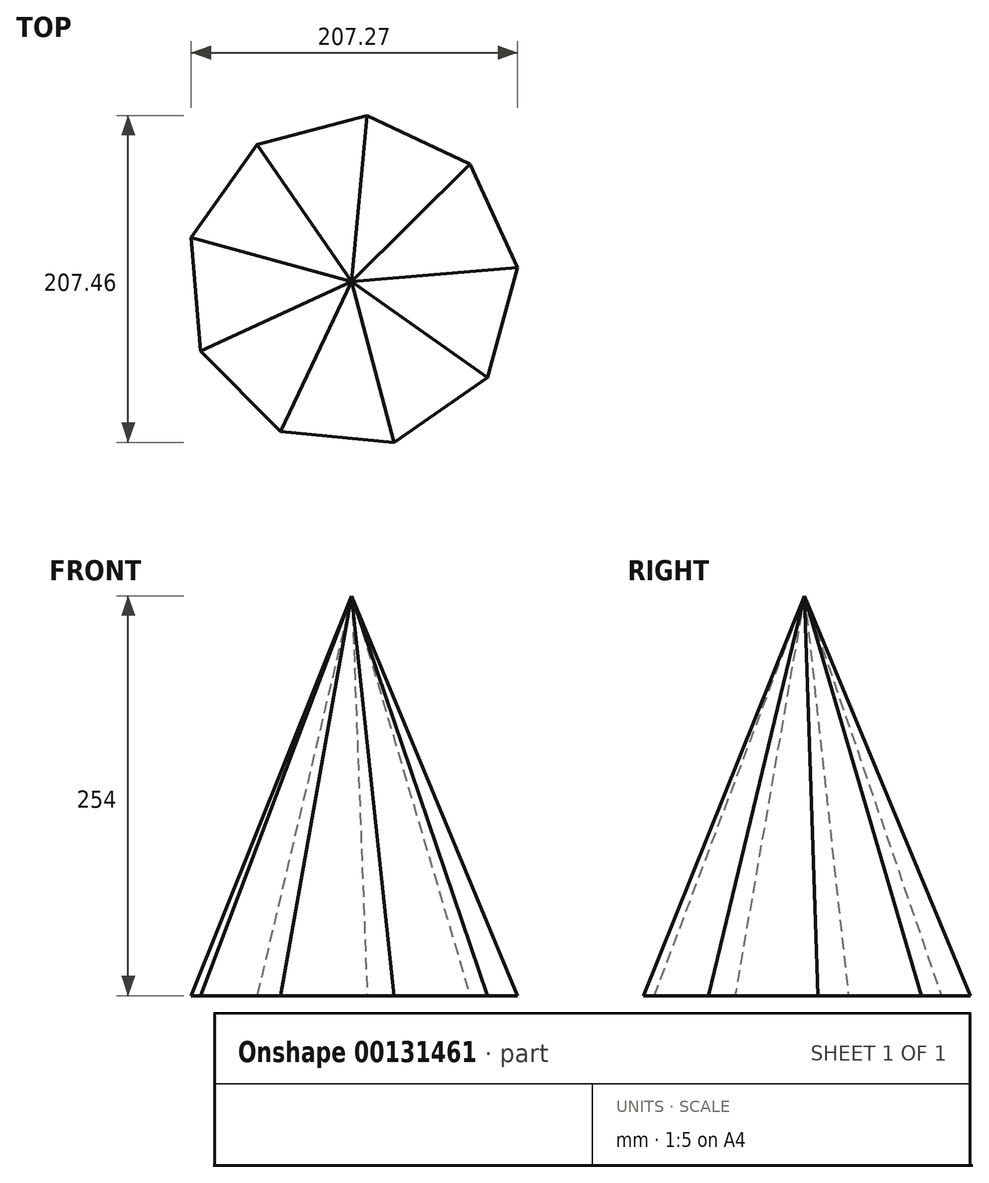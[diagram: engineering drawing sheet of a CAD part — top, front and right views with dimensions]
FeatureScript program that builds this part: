
annotation { "Feature Type Name" : "Feature", "Feature Type Description" : "" }
export const myFeature = defineFeature(function(context is Context, id is Id, definition is map)
    precondition{}
    {
        {
            var Q0;
            Q0=qCreatedBy(makeId("Top.planeOp"),FACE);
            var sketch = newSketch(context, id + "F0", { "sketchPlane" : qUnion([Q0])});
            skCircle(sketch, "E0.cCircle", {"center": v(0, 0) * mm, "radius": 105.69 * mm, "construction": true});
            skLineSegment(sketch, "E0.0", {"start": v(-101.94, 27.9) * mm, "end": v(-60.15, 86.9) * mm});
            skLineSegment(sketch, "E0.1", {"start": v(-60.15, 86.9) * mm, "end": v(9.78, 105.23) * mm});
            skLineSegment(sketch, "E0.2", {"start": v(9.78, 105.23) * mm, "end": v(75.14, 74.32) * mm});
            skLineSegment(sketch, "E0.3", {"start": v(75.14, 74.32) * mm, "end": v(105.33, 8.64) * mm});
            skLineSegment(sketch, "E0.4", {"start": v(105.33, 8.64) * mm, "end": v(86.24, -61.09) * mm});
            skLineSegment(sketch, "E0.5", {"start": v(86.24, -61.09) * mm, "end": v(26.8, -102.23) * mm});
            skLineSegment(sketch, "E0.6", {"start": v(26.8, -102.23) * mm, "end": v(-45.18, -95.54) * mm});
            skLineSegment(sketch, "E0.7", {"start": v(-45.18, -95.54) * mm, "end": v(-96.03, -44.14) * mm});
            skLineSegment(sketch, "E0.8", {"start": v(-96.03, -44.14) * mm, "end": v(-101.94, 27.9) * mm});
            skSolve(sketch);
        }
        {
            var Q0;
            Q0=qCreatedBy(makeId("Top.planeOp"),FACE);
            cPlane(context, id + "F1", {"entities" : qUnion([Q0]), "cplaneType" : CPlaneType.OFFSET, "offset" : 254 * mm, "width" : 152.4 * mm, "height" : 152.4 * mm});
        }
        {
            var Q0;
            Q0=qCreatedBy(id+"F1.planeOp",FACE);
            var sketch = newSketch(context, id + "F2", { "sketchPlane" : qUnion([Q0])});
            skPoint(sketch, "E1", {"position": v(0, 0) * mm});
            skSolve(sketch);
        }
        {
            var Q0;
            Q0=sQuery(id+"F2.wireOp",VERTEX,"E1");
            var Q1;
            Q1=makeQuery(id+"F0.imprint","IMPRINT",FACE,{"disambiguationData":[TD([[makeQuery(id+"F0.imprint","IMPRINT",EDGE,{"derivedFrom":sQuery(id+"F0.wireOp",EDGE,"E0.0")}),-1.0]])]});
            loft(context, id + "F3", {"sheetProfilesArray" : [{ "sheetProfileEntities" : qUnion([Q0]) }, { "sheetProfileEntities" : qUnion([Q1]) }]});
        }
    });
